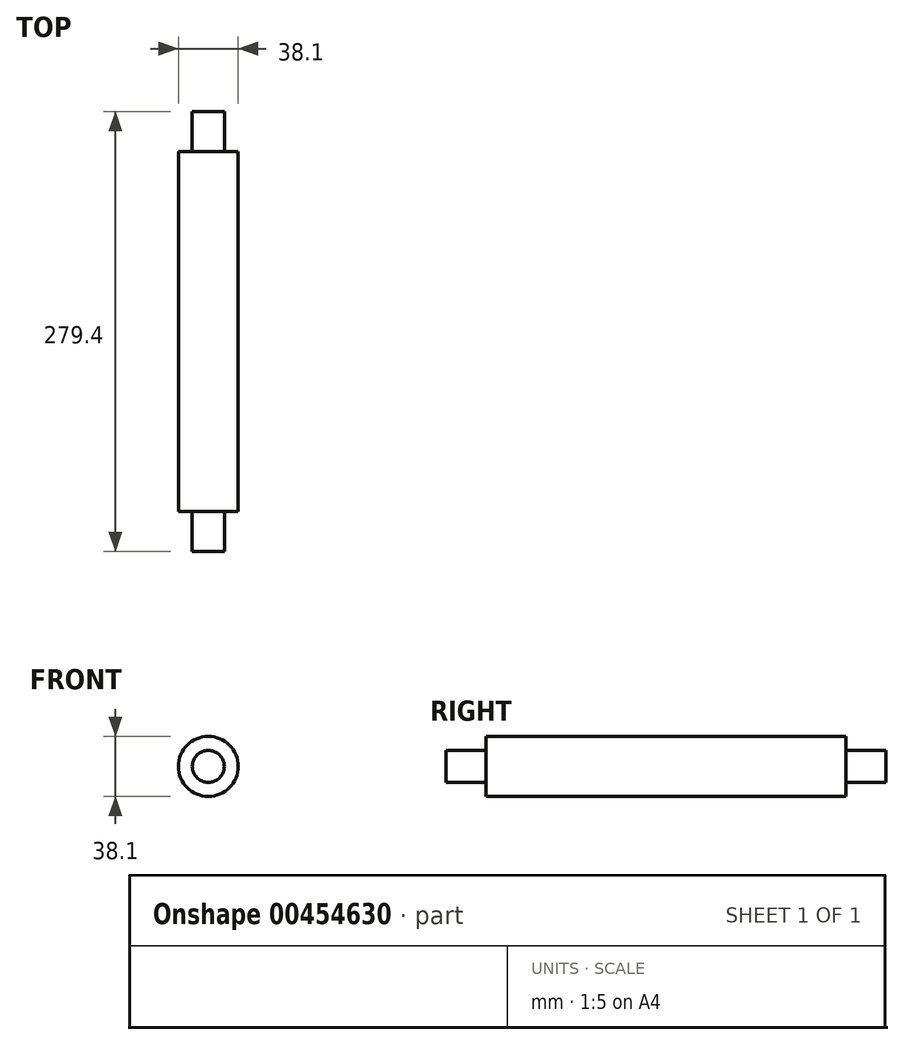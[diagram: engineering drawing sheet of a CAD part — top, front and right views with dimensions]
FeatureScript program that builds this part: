
annotation { "Feature Type Name" : "Feature", "Feature Type Description" : "" }
export const myFeature = defineFeature(function(context is Context, id is Id, definition is map)
    precondition{}
    {
        {
            var Q0;
            Q0=qCreatedBy(makeId("Front.planeOp"),FACE);
            var sketch = newSketch(context, id + "F0", { "sketchPlane" : qUnion([Q0])});
            skCircle(sketch, "E0", {"center": v(0, 0) * mm, "radius": 19.05 * mm});
            skSolve(sketch);
        }
        {
            var Q0;
            Q0 = qSketchRegion(id + "F0", true);
            extrude(context, id + "F1", {"entities" : qUnion([Q0]), "endBound" : BoundingType.SYMMETRIC, "depth" : 228.6 * mm});
        }
        {
            var Q0;
            Q0=makeQuery(id+"F1.opExtrude","CAP_FACE",FACE,{"disambiguationData":[OSD([sQuery(id+"F0.wireOp",EDGE,"E0")])],"isStart":false});
            var sketch = newSketch(context, id + "F2", { "sketchPlane" : qUnion([Q0])});
            skCircle(sketch, "E1", {"center": v(0, 0) * mm, "radius": 10.16 * mm});
            skSolve(sketch);
        }
        {
            var Q0;
            Q0 = qSketchRegion(id + "F2", true);
            extrude(context, id + "F3", {"entities" : qUnion([Q0]), "operationType" : NewBodyOperationType.ADD, "depth" : 25.4 * mm});
        }
        {
            var Q0;
            Q0=makeQuery(id+"F1.opExtrude","CAP_FACE",FACE,{"disambiguationData":[OSD([sQuery(id+"F0.wireOp",EDGE,"E0")])],"isStart":true});
            var sketch = newSketch(context, id + "F4", { "sketchPlane" : qUnion([Q0])});
            skCircle(sketch, "E2", {"center": v(0, 0) * mm, "radius": 10.16 * mm});
            skSolve(sketch);
        }
        {
            var Q0;
            Q0 = qSketchRegion(id + "F4", true);
            extrude(context, id + "F5", {"entities" : qUnion([Q0]), "operationType" : NewBodyOperationType.ADD, "depth" : 25.4 * mm});
        }
    });
